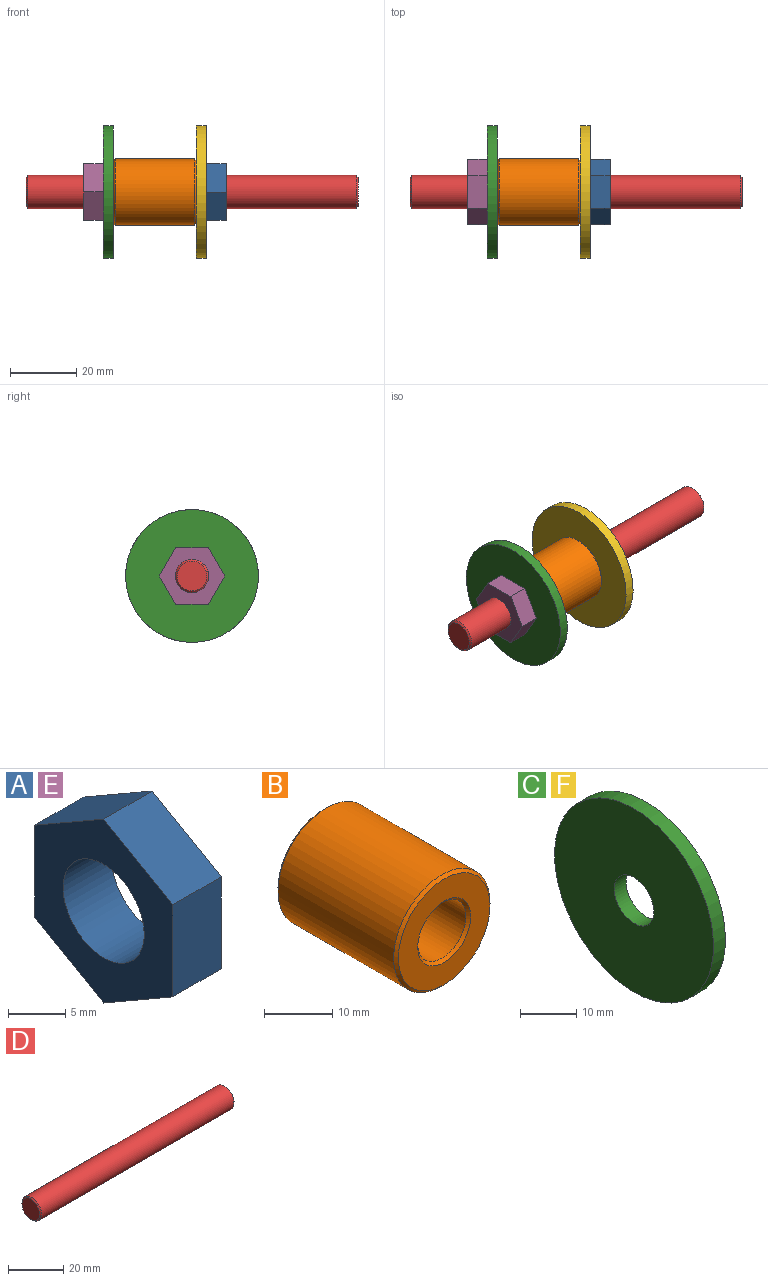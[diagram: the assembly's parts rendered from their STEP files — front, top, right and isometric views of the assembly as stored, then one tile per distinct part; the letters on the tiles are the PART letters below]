
ASSEMBLY  parts=6 mates=9
PART A: 9 faces, bbox 6x17x19.6 mm
  f0: plane 8.5x6mm, normal (0,0.5,-0.87), area 58.9mm2, adj f1,f6,f7,f8
  f1: plane 9.82x6mm, normal (0,1,0), area 58.9mm2, adj f0,f2,f7,f8
  f2: plane 8.5x6mm, normal (0,0.5,0.87), area 58.9mm2, adj f1,f3,f7,f8
  f3: plane 8.5x6mm, normal (0,-0.5,0.87), area 58.9mm2, adj f2,f4,f7,f8
  f4: plane 9.82x6mm, normal (0,-1,0), area 58.9mm2, adj f3,f6,f7,f8
  f5: cylinder r=5mm len=10mm, axis (-1,0,0), area 188.5mm2, adj f7,f8
  f6: plane 8.5x6mm, normal (0,-0.5,-0.87), area 58.9mm2, adj f0,f4,f7,f8
  f7: plane 19.63x17mm, normal (1,0,0), area 171.7mm2, adj f0,f1,f2,f3,f4,f5,f6
  f8: plane 19.63x17mm, normal (-1,0,0), area 171.7mm2, adj f0,f1,f2,f3,f4,f5,f6
PART B: 8 faces, bbox 20x25x20 mm
  f0: cylinder r=5mm len=24mm, axis (0,1,0), area 754mm2, adj f4,f6
  f1: cylinder r=10mm len=24mm, axis (0,1,0), area 1508mm2, adj f5,f7
  f2: plane 19x19mm, normal (0,-1,0), area 188.5mm2, adj f4,f5
  f3: plane 19x19mm, normal (0,1,0), area 188.5mm2, adj f6,f7
  f4: cone r=5mm half-angle=45deg, axis (0,-1,0), area 23.3mm2, adj f0,f2
  f5: cone r=9.5mm half-angle=45deg, axis (0,1,0), area 43.3mm2, adj f1,f2
  f6: cone r=5.5mm half-angle=45deg, axis (0,1,0), area 23.3mm2, adj f0,f3
  f7: cone r=10mm half-angle=45deg, axis (0,-1,0), area 43.3mm2, adj f1,f3
PART C: 4 faces, bbox 3x40x40 mm
  f0: cylinder r=5mm len=10mm, axis (-1,0,0), area 94.2mm2, adj f2,f3
  f1: cylinder r=20mm len=40mm, axis (-1,0,0), area 377mm2, adj f2,f3
  f2: plane 40x40mm, normal (1,0,0), area 1178.1mm2, adj f0,f1
  f3: plane 40x40mm, normal (-1,0,0), area 1178.1mm2, adj f0,f1
PART D: 5 faces, bbox 100x10x10 mm
  f0: cylinder r=5mm len=99mm, axis (-1,0,0), area 3110.2mm2, adj f3,f4
  f1: plane 9x9mm, normal (1,0,0), area 63.6mm2, adj f4
  f2: plane 9x9mm, normal (-1,0,0), area 63.6mm2, adj f3
  f3: cone r=5mm half-angle=45deg, axis (1,0,0), area 21.1mm2, adj f0,f2
  f4: cone r=4.5mm half-angle=45deg, axis (-1,0,0), area 21.1mm2, adj f0,f1
PART E: same geometry as A
PART F: same geometry as C
PLACE A rot(axis=(1,0,0),30.4deg) t=(54.32,0,0)mm
PLACE B rot(axis=(-0.22,0.22,0.95),93deg) t=(26.32,0,0)mm
PLACE C rot(axis=(1,0,0),42.6deg) t=(23.32,0,0)mm
PLACE D at identity fixed
PLACE E rot(axis=(-1,0,0),90deg) t=(17.32,0,0)mm
PLACE F rot(axis=(-1,0,0),59.6deg) t=(51.32,0,0)mm
MATE cylindrical B.f0 <-> D.f0  axis (-1,0,0) through (38.82,0,0)mm
MATE planar C.f1 <-> B.f1  axis (1,0,0) through (26.32,0,0)mm
MATE planar F.f1 <-> B.f1  axis (-1,0,0) through (51.32,0,0)mm
MATE cylindrical D.f0 <-> E.f5  axis (-1,0,0) through (50,0,0)mm
MATE cylindrical D.f0 <-> F.f0  axis (-1,0,0) through (50,0,0)mm
MATE cylindrical D.f0 <-> A.f5  axis (-1,0,0) through (50,0,0)mm
MATE planar C.f1 <-> E.f7  axis (-1,0,0) through (23.32,0,0)mm
MATE planar F.f1 <-> A.f5  axis (1,0,0) through (54.32,0,0)mm
MATE cylindrical C.f0 <-> D.f0  axis (-1,0,0) through (26.32,0,0)mm
